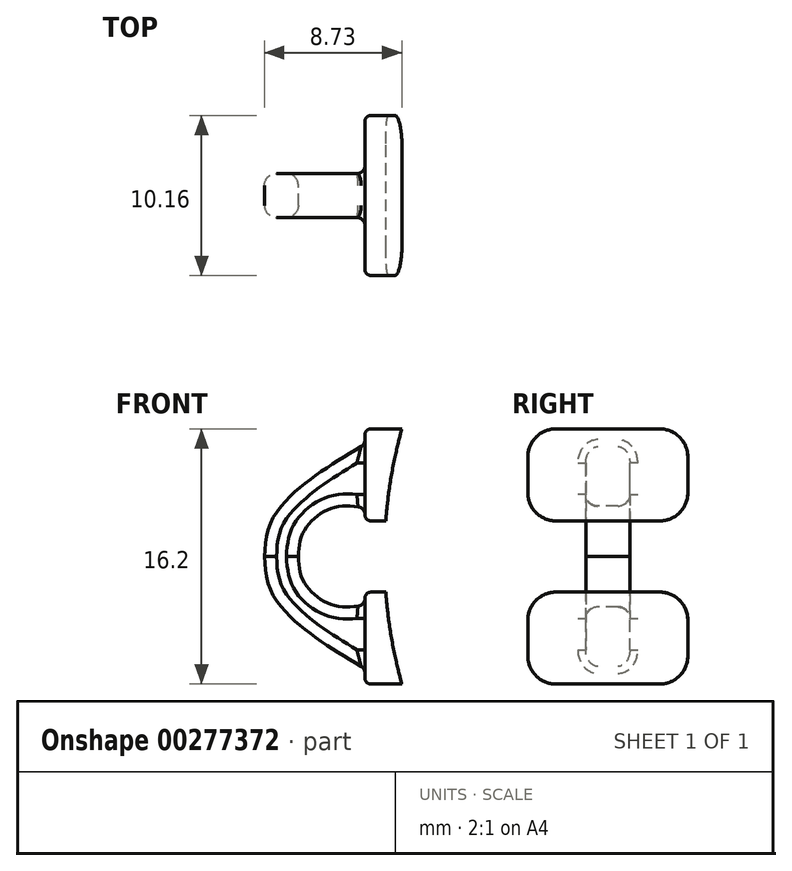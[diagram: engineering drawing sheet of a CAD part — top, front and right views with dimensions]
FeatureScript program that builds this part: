
annotation { "Feature Type Name" : "Feature", "Feature Type Description" : "" }
export const myFeature = defineFeature(function(context is Context, id is Id, definition is map)
    precondition{}
    {
        {
            var Q0;
            Q0=qCreatedBy(makeId("Front.planeOp"),FACE);
            var sketch = newSketch(context, id + "F0", { "sketchPlane" : qUnion([Q0])});
            skLineSegment(sketch, "E0", {"start": v(-29.12, -8.1) * mm, "end": v(-31.46, -8.1) * mm});
            skLineSegment(sketch, "E1", {"start": v(-31.46, -8.1) * mm, "end": v(-31.46, -7.13) * mm});
            skFitSpline(sketch, "E2", {"points": [v(-31.46, -7.13) * mm, v(-35.43, -4.51) * mm, v(-37.48, -2.1) * mm, v(-37.85, 0) * mm], "startDerivative": vector(-10.54, 6.3) * mm, "endDerivative": vector(-0.39, 7.85) * mm});
            skFitSpline(sketch, "E3", {"points": [v(-31.46, -3.1) * mm, v(-33.44, -3.1) * mm, v(-35.28, -1.74) * mm, v(-35.7, 0) * mm], "startDerivative": vector(-5.94, -0.88) * mm, "endDerivative": vector(-0.43, 5.69) * mm});
            skLineSegment(sketch, "E4", {"start": v(-31.46, -2.66) * mm, "end": v(-30.1, -2.66) * mm});
            skLineSegment(sketch, "E5.trimOffspring", {"start": v(-31.46, -3.1) * mm, "end": v(-31.46, -2.66) * mm});
            skLineSegment(sketch, "E6.MirrorCS", {"start": v(-31.46, 3.1) * mm, "end": v(-31.46, 2.66) * mm});
            skLineSegment(sketch, "E7.MirrorCS", {"start": v(-31.46, 8.1) * mm, "end": v(-31.46, 7.13) * mm});
            skLineSegment(sketch, "E8.MirrorCS", {"start": v(-29.12, 8.1) * mm, "end": v(-31.46, 8.1) * mm});
            skFitSpline(sketch, "E9.MirrorCS", {"points": [v(-31.46, 7.13) * mm, v(-35.43, 4.51) * mm, v(-37.48, 2.1) * mm, v(-37.85, 0) * mm], "startDerivative": vector(-10.54, -6.3) * mm, "endDerivative": vector(-0.39, -7.85) * mm});
            skFitSpline(sketch, "E10.MirrorCS", {"points": [v(-31.46, 3.1) * mm, v(-33.44, 3.1) * mm, v(-35.28, 1.74) * mm, v(-35.7, 0) * mm], "startDerivative": vector(-5.94, 0.88) * mm, "endDerivative": vector(-0.43, -5.69) * mm});
            skLineSegment(sketch, "E11.MirrorCS", {"start": v(-31.46, 2.66) * mm, "end": v(-30.1, 2.66) * mm});
            skArc(sketch, "E12", {"start": v(-30.1, -2.66) * mm, "mid": v(-29.74, -5.4) * mm, "end": v(-29.12, -8.1) * mm});
            skPoint(sketch, "E13.orphan", {"position": v(-29.04, 2.66) * mm});
            skPoint(sketch, "E14.orphan", {"position": v(-29.04, 8.1) * mm});
            skArc(sketch, "E15.trimOffspring", {"start": v(-29.12, 8.1) * mm, "mid": v(-29.74, 5.4) * mm, "end": v(-30.1, 2.66) * mm});
            skPoint(sketch, "E16.end.orphan", {"position": v(-29.04, -8.1) * mm});
            skPoint(sketch, "E16.start.orphan", {"position": v(-29.04, -2.66) * mm});
            skSolve(sketch);
        }
        {
            var Q0;
            Q0 = qSketchRegion(id + "F0", true);
            extrude(context, id + "F1", {"entities" : qUnion([Q0]), "depth" : 2.8 * mm, "symmetric" : true});
        }
        {
            var Q0;
            Q0=qCreatedBy(makeId("Front.planeOp"),FACE);
            var sketch = newSketch(context, id + "F2", { "sketchPlane" : qUnion([Q0])});
            skLineSegment(sketch, "E17.bottom", {"start": v(-31.46, 8.1) * mm, "end": v(-29.12, 8.1) * mm});
            skLineSegment(sketch, "E17.top", {"start": v(-31.46, -8.1) * mm, "end": v(-29.12, -8.1) * mm});
            skLineSegment(sketch, "E17.left", {"start": v(-31.46, 8.1) * mm, "end": v(-31.46, 2.26) * mm});
            skLineSegment(sketch, "E18", {"start": v(-31.46, 2.26) * mm, "end": v(-30.14, 2.26) * mm});
            skLineSegment(sketch, "E19", {"start": v(-31.46, -2.26) * mm, "end": v(-30.14, -2.26) * mm});
            skArc(sketch, "E20", {"start": v(-29.12, 8.1) * mm, "mid": v(-29.77, 5.2) * mm, "end": v(-30.14, 2.26) * mm});
            skArc(sketch, "E21.trimOffspring", {"start": v(-30.14, -2.26) * mm, "mid": v(-29.77, -5.2) * mm, "end": v(-29.12, -8.1) * mm});
            skLineSegment(sketch, "E22.trimOffspring", {"start": v(-31.46, -2.26) * mm, "end": v(-31.46, -8.1) * mm});
            skSolve(sketch);
        }
        {
            var Q0;
            Q0 = qSketchRegion(id + "F2", true);
            extrude(context, id + "F3", {"entities" : qUnion([Q0]), "operationType" : NewBodyOperationType.ADD, "depth" : 10.16 * mm, "symmetric" : true});
        }
        {
            var Q0;
            Q0=makeQuery(id+"F3.opExtrude","CAP_EDGE",EDGE,{"disambiguationData":[OSD([sQuery(id+"F2.wireOp",EDGE,"E17.bottom")])],"isStart":false});
            var Q1;
            Q1=makeQuery(id+"F3.opExtrude","CAP_EDGE",EDGE,{"disambiguationData":[OSD([sQuery(id+"F2.wireOp",EDGE,"E18")])],"isStart":false});
            var Q2;
            Q2=makeQuery(id+"F3.opExtrude","CAP_EDGE",EDGE,{"disambiguationData":[OSD([sQuery(id+"F2.wireOp",EDGE,"E17.bottom")])],"isStart":true});
            var Q3;
            Q3=makeQuery(id+"F3.opExtrude","CAP_EDGE",EDGE,{"disambiguationData":[OSD([sQuery(id+"F2.wireOp",EDGE,"E18")])],"isStart":true});
            var Q4;
            Q4=makeQuery(id+"F3.opExtrude","CAP_EDGE",EDGE,{"disambiguationData":[OSD([sQuery(id+"F2.wireOp",EDGE,"E19")])],"isStart":true});
            var Q5;
            Q5=makeQuery(id+"F3.opExtrude","CAP_EDGE",EDGE,{"disambiguationData":[OSD([sQuery(id+"F2.wireOp",EDGE,"E17.top")])],"isStart":true});
            var Q6;
            Q6=makeQuery(id+"F3.opExtrude","CAP_EDGE",EDGE,{"disambiguationData":[OSD([sQuery(id+"F2.wireOp",EDGE,"E17.top")])],"isStart":false});
            var Q7;
            Q7=makeQuery(id+"F3.opExtrude","CAP_EDGE",EDGE,{"disambiguationData":[OSD([sQuery(id+"F2.wireOp",EDGE,"E19")])],"isStart":false});
            fillet(context, id + "F4", {"entities" : qUnion([Q0, Q1, Q2, Q3, Q4, Q5, Q6, Q7]), "radius" : 1.78 * mm, "tangentPropagation" : true, "allowEdgeOverflow" : false});
        }
        {
            var Q0;
            Q0=makeQuery(id+"F1.opExtrude","CAP_EDGE",EDGE,{"disambiguationData":[OSD([sQuery(id+"F0.wireOp",EDGE,"E2")])],"isStart":false});
            var Q1;
            Q1=makeQuery(id+"F1.opExtrude","CAP_EDGE",EDGE,{"disambiguationData":[OSD([sQuery(id+"F0.wireOp",EDGE,"E9.MirrorCS")])],"isStart":false});
            var Q2;
            Q2=makeQuery(id+"F1.opExtrude","CAP_EDGE",EDGE,{"disambiguationData":[OSD([sQuery(id+"F0.wireOp",EDGE,"E9.MirrorCS")])],"isStart":true});
            var Q3;
            Q3=makeQuery(id+"F1.opExtrude","CAP_EDGE",EDGE,{"disambiguationData":[OSD([sQuery(id+"F0.wireOp",EDGE,"E2")])],"isStart":true});
            var Q4;
            Q4=makeQuery(id+"F1.opExtrude","CAP_EDGE",EDGE,{"disambiguationData":[OSD([sQuery(id+"F0.wireOp",EDGE,"E3")])],"isStart":false});
            var Q5;
            Q5=makeQuery(id+"F1.opExtrude","CAP_EDGE",EDGE,{"disambiguationData":[OSD([sQuery(id+"F0.wireOp",EDGE,"E10.MirrorCS")])],"isStart":false});
            var Q6;
            Q6=makeQuery(id+"F1.opExtrude","CAP_EDGE",EDGE,{"disambiguationData":[OSD([sQuery(id+"F0.wireOp",EDGE,"E3")])],"isStart":true});
            var Q7;
            Q7=makeQuery(id+"F1.opExtrude","CAP_EDGE",EDGE,{"disambiguationData":[OSD([sQuery(id+"F0.wireOp",EDGE,"E10.MirrorCS")])],"isStart":true});
            fillet(context, id + "F5", {"entities" : qUnion([Q0, Q1, Q2, Q3, Q4, Q5, Q6, Q7]), "radius" : 0.76 * mm, "tangentPropagation" : true, "allowEdgeOverflow" : false});
        }
        {
            var Q0;
            Q0=makeQuery(id+"F5.opFillet","BLEND_EDGE",EDGE,{"blendedFrom":[makeQuery(id+"F1.opExtrude","CAP_EDGE",EDGE,{"disambiguationData":[OSD([sQuery(id+"F0.wireOp",EDGE,"E10.MirrorCS")])],"isStart":false}),makeQuery(id+"F3.boolean.opBoolean","MERGE",FACE,{"derivedFrom":[makeQuery(id+"F1.opExtrude","SWEPT_FACE",FACE,{"disambiguationData":[OSD([sQuery(id+"F0.wireOp",EDGE,"E6.MirrorCS")])]}),makeQuery(id+"F1.opExtrude","SWEPT_FACE",FACE,{"disambiguationData":[OSD([sQuery(id+"F0.wireOp",EDGE,"E7.MirrorCS")])]}),makeQuery(id+"F3.opExtrude","SWEPT_FACE",FACE,{"disambiguationData":[OSD([sQuery(id+"F2.wireOp",EDGE,"E17.left")])]})]})],"blendedInto":[makeQuery(id+"F3.boolean.opBoolean","MERGE",FACE,{"derivedFrom":[makeQuery(id+"F1.opExtrude","SWEPT_FACE",FACE,{"disambiguationData":[OSD([sQuery(id+"F0.wireOp",EDGE,"E6.MirrorCS")])]}),makeQuery(id+"F1.opExtrude","SWEPT_FACE",FACE,{"disambiguationData":[OSD([sQuery(id+"F0.wireOp",EDGE,"E7.MirrorCS")])]}),makeQuery(id+"F3.opExtrude","SWEPT_FACE",FACE,{"disambiguationData":[OSD([sQuery(id+"F2.wireOp",EDGE,"E17.left")])]})]})]});
            var Q1;
            Q1=makeQuery(id+"F3.boolean.opBoolean","INTERSECT",EDGE,{"derivedFrom":[makeQuery(id+"F1.opExtrude","CAP_FACE",FACE,{"disambiguationData":[OSD([sQuery(id+"F0.wireOp",EDGE,"E0"),sQuery(id+"F0.wireOp",EDGE,"E1"),sQuery(id+"F0.wireOp",EDGE,"E2"),sQuery(id+"F0.wireOp",EDGE,"E3"),sQuery(id+"F0.wireOp",EDGE,"E4"),sQuery(id+"F0.wireOp",EDGE,"E5.trimOffspring"),sQuery(id+"F0.wireOp",EDGE,"E6.MirrorCS"),sQuery(id+"F0.wireOp",EDGE,"E7.MirrorCS"),sQuery(id+"F0.wireOp",EDGE,"E8.MirrorCS"),sQuery(id+"F0.wireOp",EDGE,"E9.MirrorCS"),sQuery(id+"F0.wireOp",EDGE,"E10.MirrorCS"),sQuery(id+"F0.wireOp",EDGE,"E11.MirrorCS"),sQuery(id+"F0.wireOp",EDGE,"E12"),sQuery(id+"F0.wireOp",EDGE,"E15.trimOffspring")])],"isStart":false}),makeQuery(id+"F3.opExtrude","SWEPT_FACE",FACE,{"disambiguationData":[OSD([sQuery(id+"F2.wireOp",EDGE,"E22.trimOffspring")])]})]});
            fillet(context, id + "F6", {"entities" : qUnion([Q0, Q1]), "radius" : 0.5 * mm, "tangentPropagation" : true, "allowEdgeOverflow" : false});
        }
        {
            var Q0;
            Q0=makeQuery(id+"F3.opExtrude","SWEPT_EDGE",EDGE,{"disambiguationData":[OSD([sQuery(id+"F2.wireOp",EDGE,"E17.left"),sQuery(id+"F2.wireOp",EDGE,"E18")])]});
            var Q1;
            Q1=makeQuery(id+"F4.opFillet","BLEND_EDGE",EDGE,{"blendedFrom":[makeQuery(id+"F3.opExtrude","CAP_EDGE",EDGE,{"disambiguationData":[OSD([sQuery(id+"F2.wireOp",EDGE,"E18")])],"isStart":true}),makeQuery(id+"F3.boolean.opBoolean","MERGE",FACE,{"derivedFrom":[makeQuery(id+"F1.opExtrude","SWEPT_FACE",FACE,{"disambiguationData":[OSD([sQuery(id+"F0.wireOp",EDGE,"E6.MirrorCS")])]}),makeQuery(id+"F1.opExtrude","SWEPT_FACE",FACE,{"disambiguationData":[OSD([sQuery(id+"F0.wireOp",EDGE,"E7.MirrorCS")])]}),makeQuery(id+"F3.opExtrude","SWEPT_FACE",FACE,{"disambiguationData":[OSD([sQuery(id+"F2.wireOp",EDGE,"E17.left")])]})]})],"blendedInto":[makeQuery(id+"F3.boolean.opBoolean","MERGE",FACE,{"derivedFrom":[makeQuery(id+"F1.opExtrude","SWEPT_FACE",FACE,{"disambiguationData":[OSD([sQuery(id+"F0.wireOp",EDGE,"E6.MirrorCS")])]}),makeQuery(id+"F1.opExtrude","SWEPT_FACE",FACE,{"disambiguationData":[OSD([sQuery(id+"F0.wireOp",EDGE,"E7.MirrorCS")])]}),makeQuery(id+"F3.opExtrude","SWEPT_FACE",FACE,{"disambiguationData":[OSD([sQuery(id+"F2.wireOp",EDGE,"E17.left")])]})]})]});
            var Q2;
            Q2=makeQuery(id+"F3.opExtrude","CAP_EDGE",EDGE,{"disambiguationData":[OSD([sQuery(id+"F2.wireOp",EDGE,"E17.left")])],"isStart":true});
            var Q3;
            Q3=makeQuery(id+"F4.opFillet","BLEND_EDGE",EDGE,{"blendedFrom":[makeQuery(id+"F3.opExtrude","CAP_EDGE",EDGE,{"disambiguationData":[OSD([sQuery(id+"F2.wireOp",EDGE,"E17.bottom")])],"isStart":true}),makeQuery(id+"F3.boolean.opBoolean","MERGE",FACE,{"derivedFrom":[makeQuery(id+"F1.opExtrude","SWEPT_FACE",FACE,{"disambiguationData":[OSD([sQuery(id+"F0.wireOp",EDGE,"E6.MirrorCS")])]}),makeQuery(id+"F1.opExtrude","SWEPT_FACE",FACE,{"disambiguationData":[OSD([sQuery(id+"F0.wireOp",EDGE,"E7.MirrorCS")])]}),makeQuery(id+"F3.opExtrude","SWEPT_FACE",FACE,{"disambiguationData":[OSD([sQuery(id+"F2.wireOp",EDGE,"E17.left")])]})]})],"blendedInto":[makeQuery(id+"F3.boolean.opBoolean","MERGE",FACE,{"derivedFrom":[makeQuery(id+"F1.opExtrude","SWEPT_FACE",FACE,{"disambiguationData":[OSD([sQuery(id+"F0.wireOp",EDGE,"E6.MirrorCS")])]}),makeQuery(id+"F1.opExtrude","SWEPT_FACE",FACE,{"disambiguationData":[OSD([sQuery(id+"F0.wireOp",EDGE,"E7.MirrorCS")])]}),makeQuery(id+"F3.opExtrude","SWEPT_FACE",FACE,{"disambiguationData":[OSD([sQuery(id+"F2.wireOp",EDGE,"E17.left")])]})]})]});
            var Q4;
            Q4=makeQuery(id+"F3.opExtrude","CAP_EDGE",EDGE,{"disambiguationData":[OSD([sQuery(id+"F2.wireOp",EDGE,"E17.left")])],"isStart":true});
            var Q5;
            Q5=makeQuery(id+"F3.boolean.opBoolean","MERGE",EDGE,{"derivedFrom":[makeQuery(id+"F1.opExtrude","SWEPT_EDGE",EDGE,{"disambiguationData":[OSD([sQuery(id+"F0.wireOp",EDGE,"E7.MirrorCS"),sQuery(id+"F0.wireOp",EDGE,"E8.MirrorCS")])]}),makeQuery(id+"F3.opExtrude","SWEPT_EDGE",EDGE,{"disambiguationData":[OSD([sQuery(id+"F2.wireOp",EDGE,"E17.bottom"),sQuery(id+"F2.wireOp",EDGE,"E17.left")])]})]});
            var Q6;
            Q6=makeQuery(id+"F3.opExtrude","SWEPT_EDGE",EDGE,{"disambiguationData":[OSD([sQuery(id+"F2.wireOp",EDGE,"E19"),sQuery(id+"F2.wireOp",EDGE,"E22.trimOffspring")])]});
            fillet(context, id + "F7", {"entities" : qUnion([Q0, Q1, Q2, Q3, Q4, Q5, Q6]), "radius" : 0.38 * mm, "tangentPropagation" : true, "allowEdgeOverflow" : false});
        }
    });
